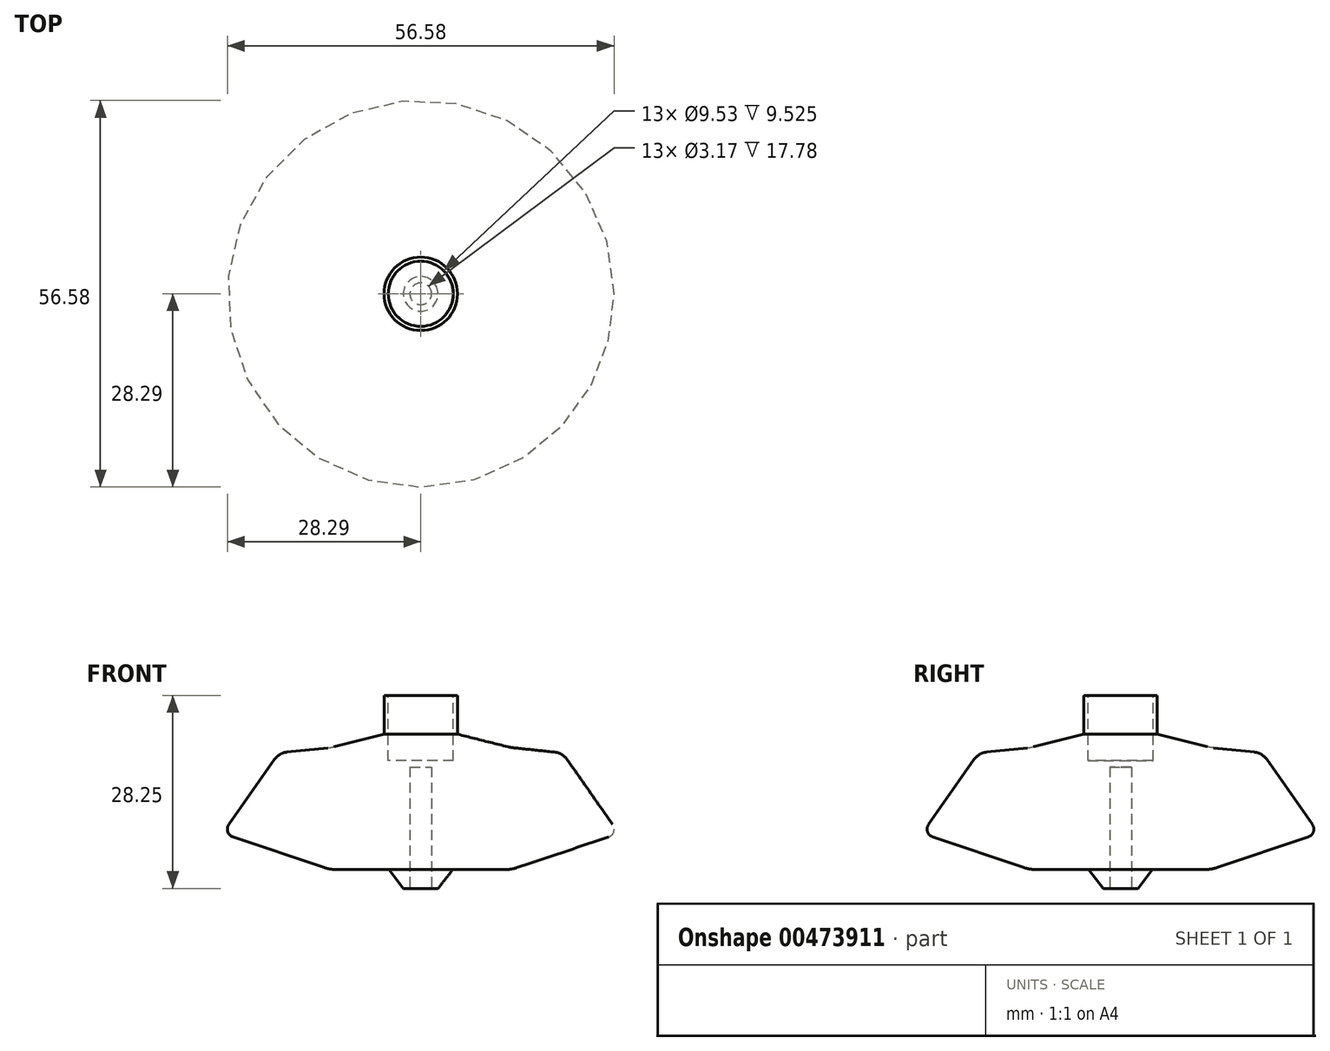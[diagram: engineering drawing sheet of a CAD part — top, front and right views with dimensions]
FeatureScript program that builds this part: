
annotation { "Feature Type Name" : "Feature", "Feature Type Description" : "" }
export const myFeature = defineFeature(function(context is Context, id is Id, definition is map)
    precondition{}
    {
        {
            var Q0;
            Q0=qCreatedBy(makeId("Front.planeOp"),FACE);
            var sketch = newSketch(context, id + "F0", { "sketchPlane" : qUnion([Q0])});
            skLineSegment(sketch, "E0", {"start": v(5.37, 22.58) * mm, "end": v(12.74, 20.73) * mm});
            skLineSegment(sketch, "E1", {"start": v(13.63, 20.57) * mm, "end": v(19.59, 19.95) * mm});
            skLineSegment(sketch, "E2", {"start": v(21.4, 18.88) * mm, "end": v(28.08, 9.35) * mm});
            skLineSegment(sketch, "E3", {"start": v(27.48, 7.53) * mm, "end": v(14.16, 3.07) * mm});
            skLineSegment(sketch, "E4", {"start": v(12.15, 2.74) * mm, "end": v(4.67, 2.74) * mm});
            skLineSegment(sketch, "E5", {"start": v(4.67, 2.74) * mm, "end": v(2.54, 0) * mm});
            skLineSegment(sketch, "E6", {"start": v(2.54, 0) * mm, "end": v(0, 0) * mm});
            skPoint(sketch, "E7.visualSharp", {"position": v(13.18, 20.62) * mm});
            skArc(sketch, "E7.filletArc", {"start": v(12.74, 20.73) * mm, "mid": v(13.18, 20.64) * mm, "end": v(13.63, 20.57) * mm});
            skPoint(sketch, "E8.visualSharp", {"position": v(29, 8.04) * mm});
            skArc(sketch, "E8.filletArc", {"start": v(27.48, 7.53) * mm, "mid": v(28.23, 8.3) * mm, "end": v(28.08, 9.35) * mm});
            skPoint(sketch, "E9.visualSharp", {"position": v(20.74, 19.83) * mm});
            skArc(sketch, "E9.filletArc", {"start": v(21.4, 18.88) * mm, "mid": v(20.61, 19.62) * mm, "end": v(19.59, 19.95) * mm});
            skPoint(sketch, "E10.visualSharp", {"position": v(13.18, 2.74) * mm});
            skArc(sketch, "E10.filletArc", {"start": v(12.15, 2.74) * mm, "mid": v(13.17, 2.82) * mm, "end": v(14.16, 3.07) * mm});
            skLineSegment(sketch, "E11", {"start": v(5.37, 22.58) * mm, "end": v(5.37, 28.25) * mm});
            skLineSegment(sketch, "E12", {"start": v(5.37, 28.25) * mm, "end": v(0, 28.25) * mm});
            skLineSegment(sketch, "E13", {"start": v(0, 28.25) * mm, "end": v(0, 0) * mm});
            skSolve(sketch);
        }
        {
            var Q0;
            Q0 = qSketchRegion(id + "F0", true);
            var Q1;
            Q1=sQuery(id+"F0.wireOp",EDGE,"E13");
            revolve(context, id + "F1", {"entities" : qUnion([Q0]), "axis" : qUnion([Q1]), "revolveType" : RevolveType.FULL});
        }
        {
            var Q0;
            Q0=makeQuery(id+"F1.opRevolve","SWEPT_FACE",FACE,{"disambiguationData":[OSD([sQuery(id+"F0.wireOp",EDGE,"E12")])]});
            var sketch = newSketch(context, id + "F2", { "sketchPlane" : qUnion([Q0])});
            skCircle(sketch, "E14", {"center": v(0, 0) * mm, "radius": 4.76 * mm});
            skSolve(sketch);
        }
        {
            var Q0;
            Q0 = qSketchRegion(id + "F2", true);
            extrude(context, id + "F3", {"entities" : qUnion([Q0]), "operationType" : NewBodyOperationType.REMOVE, "oppositeDirection" : true, "depth" : 9.52 * mm, "offsetDistance" : 25.4 * mm});
        }
        {
            var Q0;
            Q0=makeQuery(id+"F1.opRevolve","SWEPT_FACE",FACE,{"disambiguationData":[OSD([sQuery(id+"F0.wireOp",EDGE,"E6")])]});
            var sketch = newSketch(context, id + "F4", { "sketchPlane" : qUnion([Q0])});
            skCircle(sketch, "E15", {"center": v(0, 0) * mm, "radius": 1.59 * mm});
            skSolve(sketch);
        }
        {
            var Q0;
            Q0 = qSketchRegion(id + "F4", true);
            extrude(context, id + "F5", {"entities" : qUnion([Q0]), "operationType" : NewBodyOperationType.REMOVE, "oppositeDirection" : true, "depth" : 17.78 * mm, "offsetDistance" : 25.4 * mm});
        }
    });
